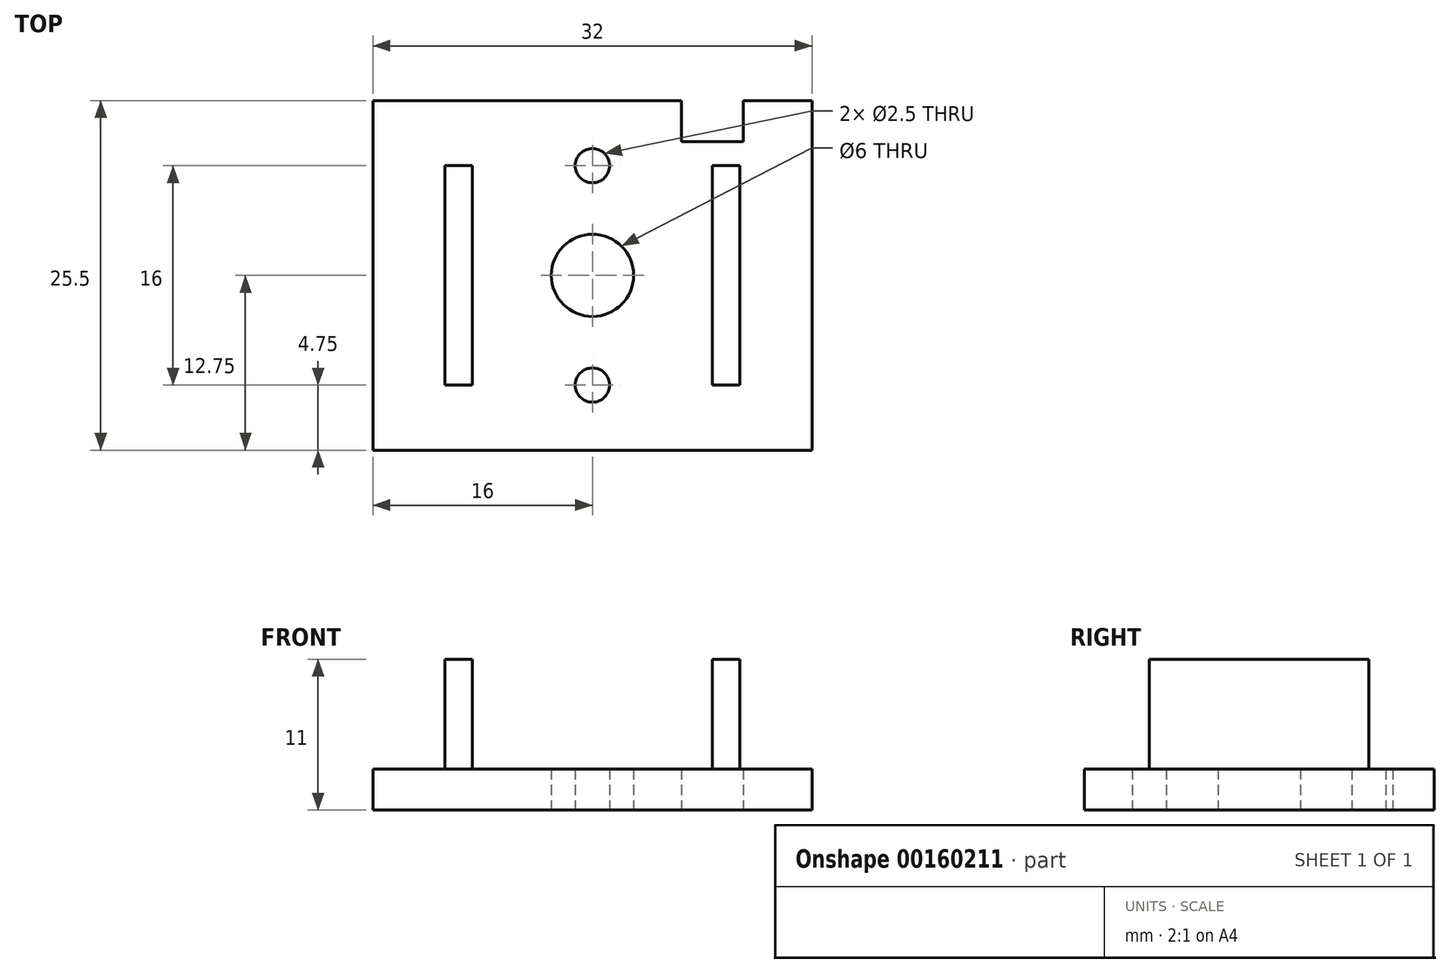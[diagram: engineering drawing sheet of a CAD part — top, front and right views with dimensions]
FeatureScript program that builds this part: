
annotation { "Feature Type Name" : "Feature", "Feature Type Description" : "" }
export const myFeature = defineFeature(function(context is Context, id is Id, definition is map)
    precondition{}
    {
        {
            var Q0;
            Q0=qCreatedBy(makeId("Top.planeOp"),FACE);
            var sketch = newSketch(context, id + "F0", { "sketchPlane" : qUnion([Q0])});
            skLineSegment(sketch, "E0.bottom", {"start": v(16, 12.75) * mm, "end": v(-16, 12.75) * mm});
            skLineSegment(sketch, "E0.top", {"start": v(16, -12.75) * mm, "end": v(-16, -12.75) * mm});
            skLineSegment(sketch, "E0.left", {"start": v(16, 12.75) * mm, "end": v(16, -12.75) * mm});
            skLineSegment(sketch, "E0.right", {"start": v(-16, 12.75) * mm, "end": v(-16, -12.75) * mm});
            skPoint(sketch, "E0.middle", {"position": v(0, 0) * mm});
            skCircle(sketch, "E1", {"center": v(0, 0) * mm, "radius": 3 * mm});
            skLineSegment(sketch, "E2", {"start": v(0, 8) * mm, "end": v(0, -8) * mm, "construction": true});
            skCircle(sketch, "E3", {"center": v(0, -8) * mm, "radius": 1.25 * mm});
            skCircle(sketch, "E4", {"center": v(0, 8) * mm, "radius": 1.25 * mm});
            skLineSegment(sketch, "E5.bottom", {"start": v(6.5, 12.75) * mm, "end": v(11, 12.75) * mm});
            skLineSegment(sketch, "E5.top", {"start": v(6.5, 9.75) * mm, "end": v(11, 9.75) * mm});
            skLineSegment(sketch, "E5.left", {"start": v(6.5, 12.75) * mm, "end": v(6.5, 9.75) * mm});
            skLineSegment(sketch, "E5.right", {"start": v(11, 12.75) * mm, "end": v(11, 9.75) * mm});
            skSolve(sketch);
        }
        {
            var Q0;
            Q0=makeQuery(id+"F0.imprint","IMPRINT",FACE,{"disambiguationData":[TD([[makeQuery(id+"F0.imprint","IMPRINT",EDGE,{"derivedFrom":sQuery(id+"F0.wireOp",EDGE,"E0.top")}),-1.0]])]});
            extrude(context, id + "F1", {"entities" : qUnion([Q0]), "depth" : 3 * mm});
        }
        {
            var Q0;
            Q0=makeQuery(id+"F1.opExtrude","CAP_FACE",FACE,{"disambiguationData":[OSD([sQuery(id+"F0.wireOp",EDGE,"E0.bottom"),sQuery(id+"F0.wireOp",EDGE,"E0.top"),sQuery(id+"F0.wireOp",EDGE,"E0.left"),sQuery(id+"F0.wireOp",EDGE,"E0.right"),sQuery(id+"F0.wireOp",EDGE,"E1"),sQuery(id+"F0.wireOp",EDGE,"E3"),sQuery(id+"F0.wireOp",EDGE,"E4"),sQuery(id+"F0.wireOp",EDGE,"E5.top"),sQuery(id+"F0.wireOp",EDGE,"E5.left"),sQuery(id+"F0.wireOp",EDGE,"E5.right")])],"isStart":false});
            var sketch = newSketch(context, id + "F2", { "sketchPlane" : qUnion([Q0])});
            skLineSegment(sketch, "E6.bottom", {"start": v(-10.75, 8) * mm, "end": v(-8.75, 8) * mm});
            skLineSegment(sketch, "E6.top", {"start": v(-10.75, -8) * mm, "end": v(-8.75, -8) * mm});
            skLineSegment(sketch, "E6.left", {"start": v(-10.75, 8) * mm, "end": v(-10.75, -8) * mm});
            skLineSegment(sketch, "E6.right", {"start": v(-8.75, 8) * mm, "end": v(-8.75, -8) * mm});
            skLineSegment(sketch, "E7.bottom", {"start": v(8.75, 8) * mm, "end": v(10.75, 8) * mm});
            skLineSegment(sketch, "E7.top", {"start": v(8.75, -8) * mm, "end": v(10.75, -8) * mm});
            skLineSegment(sketch, "E7.left", {"start": v(8.75, 8) * mm, "end": v(8.75, -8) * mm});
            skLineSegment(sketch, "E7.right", {"start": v(10.75, 8) * mm, "end": v(10.75, -8) * mm});
            skLineSegment(sketch, "E8", {"start": v(-8.75, 8) * mm, "end": v(-8.75, 12.75) * mm, "construction": true});
            skLineSegment(sketch, "E9", {"start": v(-8.75, -8) * mm, "end": v(-8.75, -12.75) * mm, "construction": true});
            skLineSegment(sketch, "E10", {"start": v(-10.75, 8) * mm, "end": v(-16, 8) * mm, "construction": true});
            skLineSegment(sketch, "E11", {"start": v(10.75, 8) * mm, "end": v(16, 8) * mm, "construction": true});
            skSolve(sketch);
        }
        {
            var Q0;
            Q0 = qSketchRegion(id + "F2", true);
            extrude(context, id + "F3", {"entities" : qUnion([Q0]), "operationType" : NewBodyOperationType.ADD, "depth" : 8 * mm});
        }
    });
